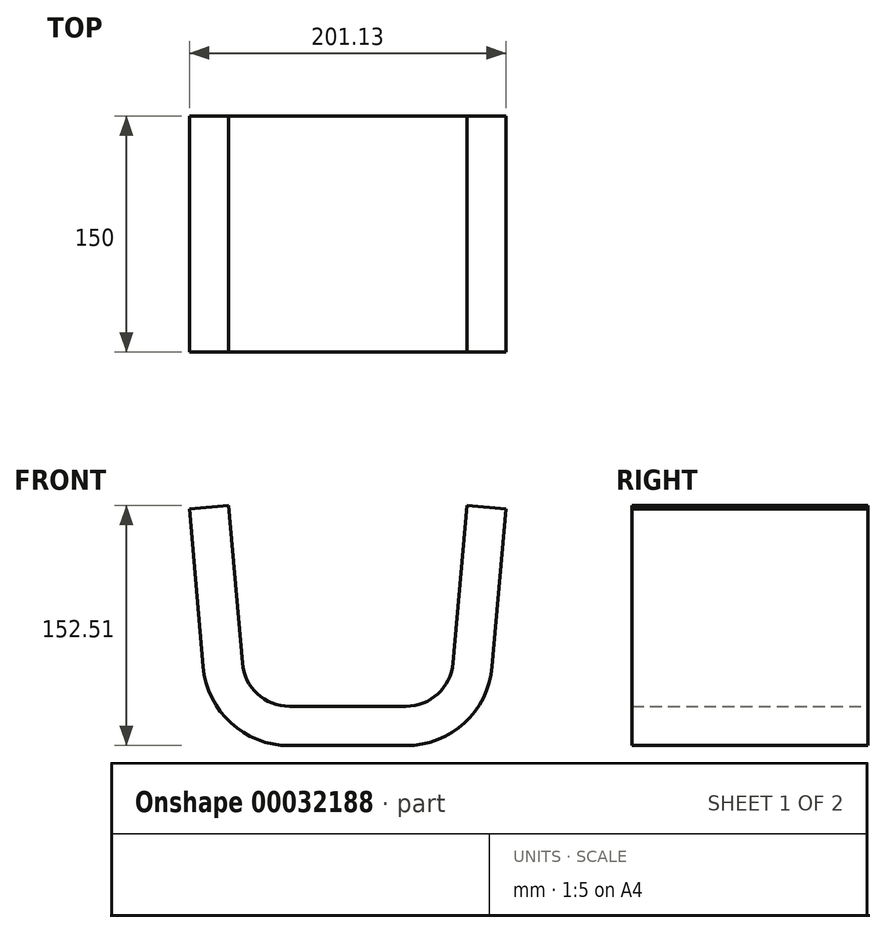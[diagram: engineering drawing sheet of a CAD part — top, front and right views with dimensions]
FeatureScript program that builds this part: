
annotation { "Feature Type Name" : "Feature", "Feature Type Description" : "" }
export const myFeature = defineFeature(function(context is Context, id is Id, definition is map)
    precondition{}
    {
        {
            var Q0;
            Q0=qCreatedBy(makeId("Front.planeOp"),FACE);
            var sketch = newSketch(context, id + "F0", { "sketchPlane" : qUnion([Q0])});
            skLineSegment(sketch, "E0", {"start": v(-66.04, 127.51) * mm, "end": v(-54.89, 0) * mm});
            skLineSegment(sketch, "E1", {"start": v(-54.89, 0) * mm, "end": v(74.11, 0) * mm});
            skLineSegment(sketch, "E2", {"start": v(74.11, 0) * mm, "end": v(85.27, 127.51) * mm});
            skLineSegment(sketch, "E3", {"start": v(-66.04, 127.51) * mm, "end": v(-90.95, 125.33) * mm});
            skLineSegment(sketch, "E4", {"start": v(-90.95, 125.33) * mm, "end": v(-77.8, -25) * mm});
            skLineSegment(sketch, "E5", {"start": v(-77.8, -25) * mm, "end": v(97.02, -25) * mm});
            skLineSegment(sketch, "E6", {"start": v(97.02, -25) * mm, "end": v(110.18, 125.33) * mm});
            skLineSegment(sketch, "E7", {"start": v(85.27, 127.51) * mm, "end": v(110.18, 125.33) * mm});
            skSolve(sketch);
        }
        {
            var Q0;
            Q0 = qSketchRegion(id + "F0", true);
            extrude(context, id + "F1", {"entities" : qUnion([Q0]), "depth" : 150 * mm});
        }
        {
            var Q0;
            Q0=makeQuery(id+"F1.opExtrude","SWEPT_EDGE",EDGE,{"disambiguationData":[OSD([sQuery(id+"F0.wireOp",EDGE,"E0"),sQuery(id+"F0.wireOp",EDGE,"E1")])]});
            var Q1;
            Q1=makeQuery(id+"F1.opExtrude","SWEPT_EDGE",EDGE,{"disambiguationData":[OSD([sQuery(id+"F0.wireOp",EDGE,"E1"),sQuery(id+"F0.wireOp",EDGE,"E2")])]});
            fillet(context, id + "F2", {"entities" : qUnion([Q0, Q1]), "radius" : 30 * mm, "tangentPropagation" : true, "allowEdgeOverflow" : false});
        }
        {
            var Q0;
            Q0=makeQuery(id+"F1.opExtrude","SWEPT_EDGE",EDGE,{"disambiguationData":[OSD([sQuery(id+"F0.wireOp",EDGE,"E4"),sQuery(id+"F0.wireOp",EDGE,"E5")])]});
            var Q1;
            Q1=makeQuery(id+"F1.opExtrude","SWEPT_EDGE",EDGE,{"disambiguationData":[OSD([sQuery(id+"F0.wireOp",EDGE,"E5"),sQuery(id+"F0.wireOp",EDGE,"E6")])]});
            fillet(context, id + "F3", {"entities" : qUnion([Q0, Q1]), "radius" : 55 * mm, "tangentPropagation" : true, "allowEdgeOverflow" : false});
        }
    });
